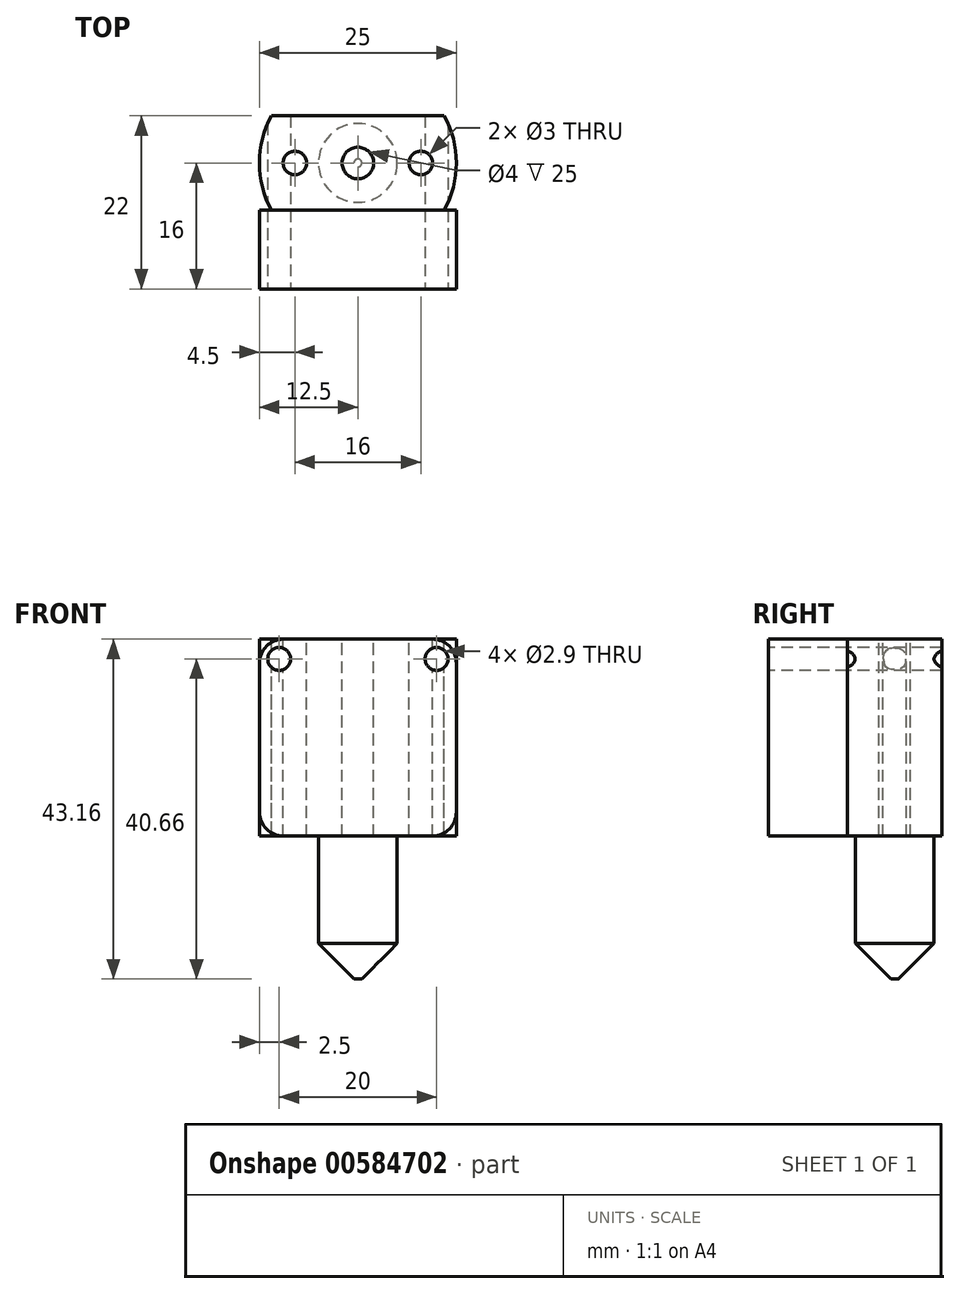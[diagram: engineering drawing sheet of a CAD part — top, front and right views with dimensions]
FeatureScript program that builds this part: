
annotation { "Feature Type Name" : "Feature", "Feature Type Description" : "" }
export const myFeature = defineFeature(function(context is Context, id is Id, definition is map)
    precondition{}
    {
        {
            var Q0;
            Q0=qCreatedBy(makeId("Front.planeOp"),FACE);
            var sketch = newSketch(context, id + "F0", { "sketchPlane" : qUnion([Q0])});
            skLineSegment(sketch, "E0.bottom", {"start": v(12.5, 0) * mm, "end": v(-12.5, 0) * mm});
            skLineSegment(sketch, "E0.top", {"start": v(12.5, -25) * mm, "end": v(-12.5, -25) * mm});
            skLineSegment(sketch, "E0.left", {"start": v(12.5, 0) * mm, "end": v(12.5, -25) * mm});
            skLineSegment(sketch, "E0.right", {"start": v(-12.5, 0) * mm, "end": v(-12.5, -25) * mm});
            skPoint(sketch, "E0.middle", {"position": v(0, -12.5) * mm});
            skSolve(sketch);
        }
        {
            var Q0;
            Q0=qSketchRegion(id+"F0",true);
            extrude(context, id + "F1", {"entities" : qUnion([Q0]), "endBound" : BoundingType.SYMMETRIC, "depth" : 12 * mm});
        }
        {
            var Q0;
            Q0=qCreatedBy(makeId("Front.planeOp"),FACE);
            var sketch = newSketch(context, id + "F2", { "sketchPlane" : qUnion([Q0])});
            skLineSegment(sketch, "E1", {"start": v(0, -25) * mm, "end": v(0, -43.16) * mm});
            skLineSegment(sketch, "E2", {"start": v(0, -43.16) * mm, "end": v(0.5, -43.16) * mm});
            skLineSegment(sketch, "E3", {"start": v(0.5, -43.16) * mm, "end": v(5, -38.66) * mm});
            skLineSegment(sketch, "E4", {"start": v(5, -38.66) * mm, "end": v(5, -25) * mm});
            skLineSegment(sketch, "E5", {"start": v(5, -25) * mm, "end": v(0, -25) * mm});
            skSolve(sketch);
        }
        {
            var Q0;
            Q0=qSketchRegion(id+"F2",true);
            var Q1;
            Q1=sQuery(id+"F2.wireOp",EDGE,"E1");
            revolve(context, id + "F3", {"operationType" : NewBodyOperationType.ADD, "entities" : qUnion([Q0]), "axis" : qUnion([Q1]), "revolveType" : RevolveType.FULL});
        }
        {
            var Q0;
            Q0=makeQuery(id+"F1.opExtrude","SWEPT_FACE",FACE,{"disambiguationData":[OSD([sQuery(id+"F0.wireOp",EDGE,"E0.bottom")])]});
            var sketch = newSketch(context, id + "F4", { "sketchPlane" : qUnion([Q0])});
            skCircle(sketch, "E6", {"center": v(0, 0) * mm, "radius": 2 * mm});
            skCircle(sketch, "E7", {"center": v(-8, 0) * mm, "radius": 1.5 * mm});
            skCircle(sketch, "E8", {"center": v(8, 0) * mm, "radius": 1.5 * mm});
            skLineSegment(sketch, "E9", {"start": v(-8, 0) * mm, "end": v(0, 0) * mm, "construction": true});
            skLineSegment(sketch, "E10", {"start": v(8, 0) * mm, "end": v(0, 0) * mm, "construction": true});
            skCircle(sketch, "E11", {"center": v(0, 0) * mm, "radius": 12.5 * mm});
            skCircle(sketch, "E12", {"center": v(0, 0) * mm, "radius": 26.2 * mm});
            skSolve(sketch);
        }
        {
            var Q0;
            Q0=makeQuery(id+"F4.imprint","IMPRINT",FACE,{"disambiguationData":[TD([[makeQuery(id+"F4.imprint","IMPRINT",EDGE,{"derivedFrom":sQuery(id+"F4.wireOp",EDGE,"E7")}),1.0]])]});
            var Q1;
            Q1=makeQuery(id+"F4.imprint","IMPRINT",FACE,{"disambiguationData":[TD([[makeQuery(id+"F4.imprint","IMPRINT",EDGE,{"derivedFrom":sQuery(id+"F4.wireOp",EDGE,"E6")}),1.0]])]});
            var Q2;
            Q2=makeQuery(id+"F4.imprint","IMPRINT",FACE,{"disambiguationData":[TD([[makeQuery(id+"F4.imprint","IMPRINT",EDGE,{"derivedFrom":sQuery(id+"F4.wireOp",EDGE,"E8")}),1.0]])]});
            var Q3;
            Q3=makeQuery(id+"F4.imprint","IMPRINT",FACE,{"disambiguationData":[TD([[makeQuery(id+"F4.imprint","IMPRINT",EDGE,{"derivedFrom":sQuery(id+"F4.wireOp",EDGE,"E12")}),1.0]])]});
            var Q4;
            {var subQ0=sQuery(id+"F4.wireOp",EDGE,"E11");var subQ1=sQuery(id+"F0.wireOp",EDGE,"E0.bottom");var subQ4=makeQuery(id+"F1.opExtrude","CAP_EDGE",EDGE,{"disambiguationData":[OSD([subQ1])],"isStart":false});var subQ5=makeQuery(id+"F4.imprint","INTERSECT",VERTEX,{"disambiguationData":[OD(1.0)],"derivedFrom":[subQ4,subQ0]});Q4=makeQuery(id+"F4.imprint","IMPRINT",FACE,{"disambiguationData":[TD([[makeQuery(id+"F4.imprint","IMPRINT",EDGE,{"disambiguationData":[TD([[subQ5,-1.0]])],"derivedFrom":subQ0}),-1.0]])]});}
            var Q5;
            {var subQ0=sQuery(id+"F4.wireOp",EDGE,"E11");var subQ1=sQuery(id+"F0.wireOp",EDGE,"E0.bottom");var subQ2=makeQuery(id+"F1.opExtrude","CAP_EDGE",EDGE,{"disambiguationData":[OSD([subQ1])],"isStart":true});var subQ3=makeQuery(id+"F4.imprint","INTERSECT",VERTEX,{"disambiguationData":[OD(0.0)],"derivedFrom":[subQ2,subQ0]});Q5=makeQuery(id+"F4.imprint","IMPRINT",FACE,{"disambiguationData":[TD([[makeQuery(id+"F4.imprint","IMPRINT",EDGE,{"disambiguationData":[TD([[subQ3,1.0]])],"derivedFrom":subQ0}),-1.0]])]});}
            var Q6;
            {var subQ0=sQuery(id+"F4.wireOp",EDGE,"E11");var subQ1=sQuery(id+"F0.wireOp",EDGE,"E0.bottom");var subQ2=makeQuery(id+"F1.opExtrude","CAP_EDGE",EDGE,{"disambiguationData":[OSD([subQ1])],"isStart":true});var subQ3=makeQuery(id+"F4.imprint","INTERSECT",VERTEX,{"disambiguationData":[OD(1.0)],"derivedFrom":[subQ2,subQ0]});Q6=makeQuery(id+"F4.imprint","IMPRINT",FACE,{"disambiguationData":[TD([[makeQuery(id+"F4.imprint","IMPRINT",EDGE,{"disambiguationData":[TD([[subQ3,-1.0]])],"derivedFrom":subQ0}),-1.0]])]});}
            var Q7;
            {var subQ0=sQuery(id+"F4.wireOp",EDGE,"E11");var subQ1=sQuery(id+"F0.wireOp",EDGE,"E0.bottom");var subQ4=makeQuery(id+"F1.opExtrude","CAP_EDGE",EDGE,{"disambiguationData":[OSD([subQ1])],"isStart":false});var subQ5=makeQuery(id+"F4.imprint","INTERSECT",VERTEX,{"disambiguationData":[OD(0.0)],"derivedFrom":[subQ4,subQ0]});Q7=makeQuery(id+"F4.imprint","IMPRINT",FACE,{"disambiguationData":[TD([[makeQuery(id+"F4.imprint","IMPRINT",EDGE,{"disambiguationData":[TD([[subQ5,1.0]])],"derivedFrom":subQ0}),-1.0]])]});}
            extrude(context, id + "F5", {"entities" : qUnion([Q0, Q1, Q2, Q3, Q4, Q5, Q6, Q7]), "operationType" : NewBodyOperationType.REMOVE, "oppositeDirection" : true, "depth" : 25 * mm});
        }
        {
            var Q0;
            Q0=makeQuery(id+"F1.opExtrude","CAP_FACE",FACE,{"disambiguationData":[OSD([sQuery(id+"F0.wireOp",EDGE,"E0.bottom"),sQuery(id+"F0.wireOp",EDGE,"E0.top"),sQuery(id+"F0.wireOp",EDGE,"E0.left"),sQuery(id+"F0.wireOp",EDGE,"E0.right")])],"isStart":false});
            var sketch = newSketch(context, id + "F6", { "sketchPlane" : qUnion([Q0])});
            skLineSegment(sketch, "E13.0", {"start": v(12.5, 0) * mm, "end": v(-12.5, 0) * mm});
            skLineSegment(sketch, "E13.1", {"start": v(-12.5, 0) * mm, "end": v(-12.5, -25) * mm});
            skLineSegment(sketch, "E13.2", {"start": v(12.5, 0) * mm, "end": v(12.5, -25) * mm});
            skLineSegment(sketch, "E13.3", {"start": v(12.5, -25) * mm, "end": v(-12.5, -25) * mm});
            skSolve(sketch);
        }
        {
            var Q0;
            {var subQ2=sQuery(id+"F6.wireOp",EDGE,"E13.1");Q0=makeQuery(id+"F6.imprint","IMPRINT",FACE,{"disambiguationData":[TD([[makeQuery(id+"F6.imprint","IMPRINT",EDGE,{"derivedFrom":subQ2}),1.0]])]});}
            var Q1;
            {var subQ1=makeQuery(id+"F5.opExtrude","SWEPT_FACE",FACE,{"disambiguationData":[OSD([sQuery(id+"F4.wireOp",EDGE,"E11")])]});var subQ2=makeQuery(id+"F1.opExtrude","CAP_FACE",FACE,{"disambiguationData":[OSD([sQuery(id+"F0.wireOp",EDGE,"E0.bottom"),sQuery(id+"F0.wireOp",EDGE,"E0.top"),sQuery(id+"F0.wireOp",EDGE,"E0.left"),sQuery(id+"F0.wireOp",EDGE,"E0.right")])],"isStart":false});var subQ3=makeQuery(id+"F5.boolean.opBoolean","INTERSECT",EDGE,{"disambiguationData":[OD(0.0)],"derivedFrom":[subQ2,subQ1]});Q1=makeQuery(id+"F6.imprint","IMPRINT",FACE,{"disambiguationData":[TD([[makeQuery(id+"F6.imprint","IMPRINT",EDGE,{"derivedFrom":subQ3}),1.0]])]});}
            var Q2;
            {var subQ2=sQuery(id+"F6.wireOp",EDGE,"E13.2");Q2=makeQuery(id+"F6.imprint","IMPRINT",FACE,{"disambiguationData":[TD([[makeQuery(id+"F6.imprint","IMPRINT",EDGE,{"derivedFrom":subQ2}),-1.0]])]});}
            extrude(context, id + "F7", {"entities" : qUnion([Q0, Q1, Q2]), "depth" : 10 * mm});
        }
        {
            var Q0;
            Q0=makeQuery(id+"F7.opExtrude","CAP_FACE",FACE,{"disambiguationData":[OSD([sQuery(id+"F6.wireOp",EDGE,"E13.0"),sQuery(id+"F6.wireOp",EDGE,"E13.1"),sQuery(id+"F6.wireOp",EDGE,"E13.2"),sQuery(id+"F6.wireOp",EDGE,"E13.3")])],"isStart":false});
            var sketch = newSketch(context, id + "F8", { "sketchPlane" : qUnion([Q0])});
            skLineSegment(sketch, "E14.bottom", {"start": v(10, -2.5) * mm, "end": v(-10, -2.5) * mm, "construction": true});
            skLineSegment(sketch, "E14.top", {"start": v(10, -22.5) * mm, "end": v(-10, -22.5) * mm, "construction": true});
            skLineSegment(sketch, "E14.left", {"start": v(10, -2.5) * mm, "end": v(10, -22.5) * mm, "construction": true});
            skLineSegment(sketch, "E14.right", {"start": v(-10, -2.5) * mm, "end": v(-10, -22.5) * mm, "construction": true});
            skPoint(sketch, "E14.middle", {"position": v(0, -12.5) * mm});
            skLineSegment(sketch, "E15", {"start": v(-12.5, -25) * mm, "end": v(12.5, 0) * mm, "construction": true});
            skCircle(sketch, "E16", {"center": v(-10, -2.5) * mm, "radius": 1.45 * mm});
            skCircle(sketch, "E17", {"center": v(10, -2.5) * mm, "radius": 1.45 * mm});
            skSolve(sketch);
        }
        {
            var Q0;
            Q0=qSketchRegion(id+"F8",true);
            extrude(context, id + "F9", {"entities" : qUnion([Q0]), "operationType" : NewBodyOperationType.REMOVE, "oppositeDirection" : true, "depth" : 25 * mm});
        }
        {
            var Q0;
            Q0=makeQuery(id+"F7.opExtrude","SWEPT_EDGE",EDGE,{"disambiguationData":[OSD([sQuery(id+"F6.wireOp",EDGE,"E13.0"),sQuery(id+"F6.wireOp",EDGE,"E13.2")])]});
            var Q1;
            Q1=makeQuery(id+"F7.opExtrude","SWEPT_EDGE",EDGE,{"disambiguationData":[OSD([sQuery(id+"F6.wireOp",EDGE,"E13.0"),sQuery(id+"F6.wireOp",EDGE,"E13.1")])]});
            var Q2;
            Q2=makeQuery(id+"F7.opExtrude","SWEPT_EDGE",EDGE,{"disambiguationData":[OSD([sQuery(id+"F6.wireOp",EDGE,"E13.1"),sQuery(id+"F6.wireOp",EDGE,"E13.3")])]});
            var Q3;
            Q3=makeQuery(id+"F7.opExtrude","SWEPT_EDGE",EDGE,{"disambiguationData":[OSD([sQuery(id+"F6.wireOp",EDGE,"E13.2"),sQuery(id+"F6.wireOp",EDGE,"E13.3")])]});
            fillet(context, id + "F10", {"entities" : qUnion([Q0, Q1, Q2, Q3]), "radius" : 3 * mm, "tangentPropagation" : true, "allowEdgeOverflow" : false});
        }
    });
